# Revit family: Diverter_Valve_Trim-Two_Way-Grohe-Concetto-29108_Series
name_source: partatom
category: Plumbing Fixtures
revit_build: Autodesk Revit 2018 (Build: 20170223_1515(x64)
units: mm (PartAtom-declared; Revit-internal decimal feet)

## family parameters
Cut with Voids When Loaded = No
Host = Face
OmniClass Number = 23.45.05.14.17
OmniClass Title = Showers
Part Type = Normal
Room Calculation Point = No
Round Connector Dimension = Use Diameter
Shared = Yes

## types (2) — shared parameters
ADA Compliant = Yes
Assembly Code = D2010710
CW Connection = No
CWFU = 3
Default Elevation = 44"
Description = Concetto 2-Way Diverter Trim (Shower head/Hand Shower)
HW Connection = No
HWFU = 3
Height = 4 13/16"
IAPMO Compliance = ICC/ANSI A117.1
Installation Type = Wall Mounted
Length = 2 5/8"
Manufacturer = Grohe
Price = Prices may vary. Please consult Manufacturer Representative for most up-to-date price list.
Product Documentation Link = https://americanstandard.box.com
Product Page URL = https://www.grohe.us
Revised Date = 07/12/2021
Tempered Water Connection = Yes
Tempered Water Connection Diameter = 1/2"
Type Comments = GROHE StarLight scratch and tarnish-resistant surfaces for a lifetime of beauty, CALGreen and ADA compliant metal lever handle for shower head and hand shower outlets compatible with 0.5inch NPT 2-way diverter rough-in valves (29900 or 2990), and a metal wall escutcheon.
URL = https://www.grohe.us
Vent Connection = No
WFU = 4
Waste Connection = No
Width = 3 1/8"

## per-type parameters (varying)
| type | Finish | Material |
| 29108001 | Metal-Grohe-001-StarLight Chrome | Metal-Grohe-001-StarLight Chrome |
| 29108EN1 | Metal-Grohe-EN1-Brushed Nickel Infinity Finish | Metal-Grohe-EN1-Brushed Nickel Infinity Finish |

note: column(s) folded — value = type name in every type: Model

## geometry (parser evidence)
native form markers: Sweep x5
no freeform markers — native parametric forms only
